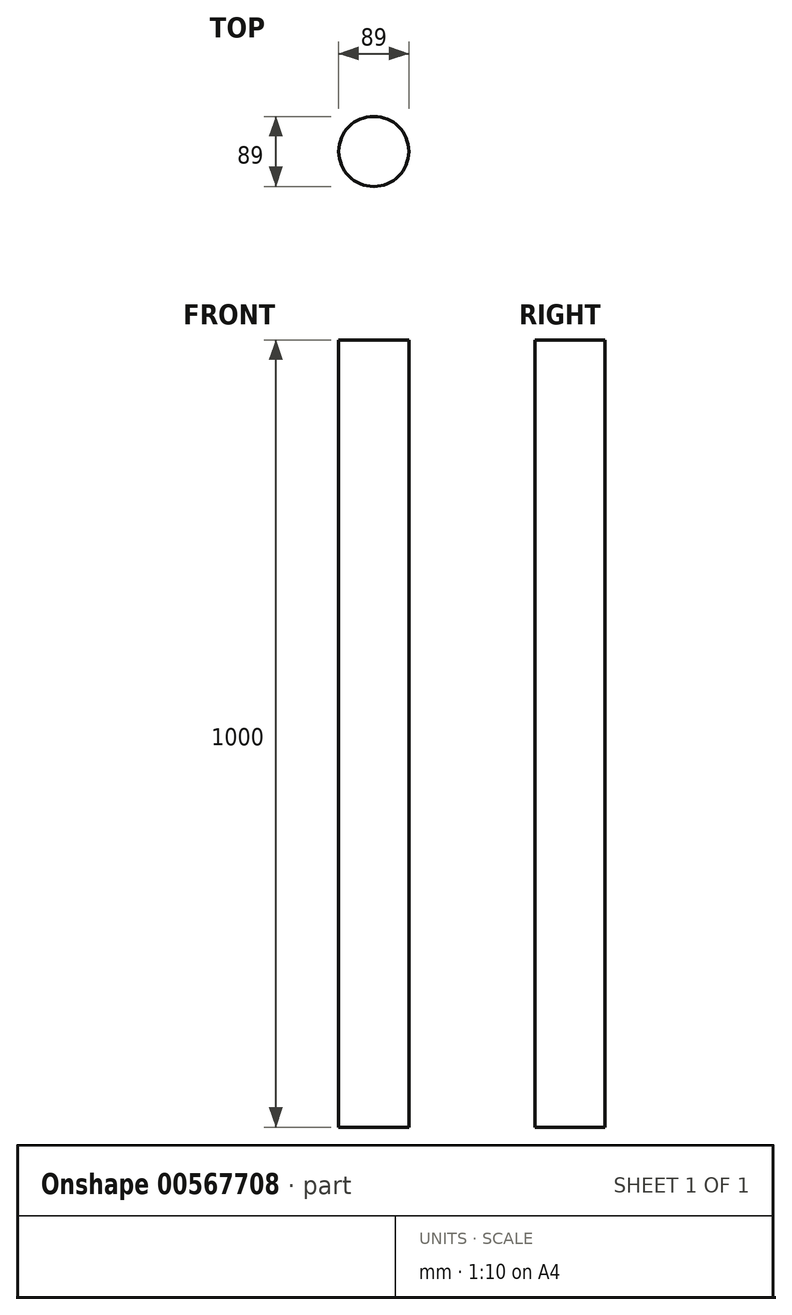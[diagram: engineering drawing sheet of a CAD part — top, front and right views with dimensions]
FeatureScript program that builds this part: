
annotation { "Feature Type Name" : "Feature", "Feature Type Description" : "" }
export const myFeature = defineFeature(function(context is Context, id is Id, definition is map)
    precondition{}
    {
        {
            var Q0;
            Q0=qCreatedBy(makeId("Top.planeOp"),FACE);
            var sketch = newSketch(context, id + "F0", { "sketchPlane" : qUnion([Q0])});
            skCircle(sketch, "E0", {"center": v(0, 0) * mm, "radius": 44.5 * mm});
            skSolve(sketch);
        }
        {
            var Q0;
            Q0=makeQuery(id+"F0.imprint","IMPRINT",FACE,{"disambiguationData":[TD([[makeQuery(id+"F0.imprint","IMPRINT",EDGE,{"derivedFrom":sQuery(id+"F0.wireOp",EDGE,"E0")}),1.0]])]});
            extrude(context, id + "F1", {"entities" : qUnion([Q0]), "depth" : 1000 * mm, "offsetDistance" : 25 * mm});
        }
    });
